# Revit family: RF-3
name_source: partatom
category: Generic Models
revit_build: Autodesk Revit 2018 (Build: 20170223_1515(x64)
units: mm (PartAtom-declared; Revit-internal decimal feet)

## family parameters
Always vertical = Yes
Can host rebar = No
Cut with Voids When Loaded = No
Part Type = Normal
Room Calculation Point = No
Round Connector Dimension = Use Diameter
Shared = No
Work Plane-Based = No

## types (9) — shared parameters
Enclosure Height = 11 3/32"
Enclosure Width = 14 7/32"
Manufacturer = Anemostat
URL = www.anemostat-hvac.com

## per-type parameters (varying)
| type | Diameter | Duct Size | Length | Model | Radius |
| 05" Inlet | 5" | 5" | 20 5/16" | RF-3 | 2" |
| 06" Inlet | 6" | 6" | 20 5/16" | XAFT | 3" |
| 07" Inlet | 7" | 7" | 20 5/16" | XAFT | 3" |
| 08" Inlet | 8" | 8" | 20 5/16" | XAFT | 4" |
| 09" Inlet | 9" | 9" | 20 5/16" | XAFT | 4" |
| 10" Inlet | 10" | 10" | 20 5/16" | XAFT | 5" |
| 12" Inlet | 12" | 12" | 23 29/32" | XAFT | 6" |
| 14" Inlet | 14" | 14" | 23 29/32" | XAFT | 7" |
| 16" Inlet | 16" | 16" | 23 29/32" | XAFT | 8" |

## geometry (parser evidence)
native form markers: Sweep x2
no freeform markers — native parametric forms only
